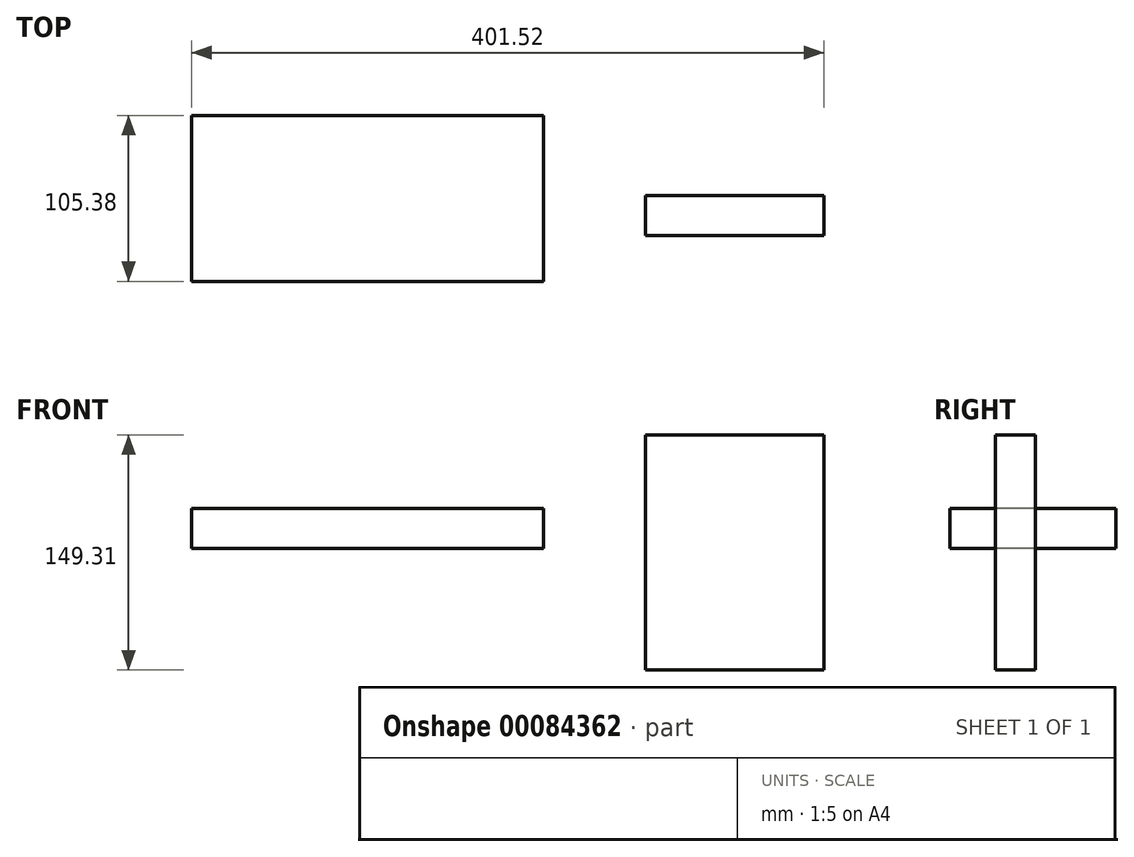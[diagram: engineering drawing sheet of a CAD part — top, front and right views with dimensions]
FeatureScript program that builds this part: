
annotation { "Feature Type Name" : "Feature", "Feature Type Description" : "" }
export const myFeature = defineFeature(function(context is Context, id is Id, definition is map)
    precondition{}
    {
        {
            var Q0;
            Q0=qCreatedBy(makeId("Top.planeOp"),FACE);
            var sketch = newSketch(context, id + "F0", { "sketchPlane" : qUnion([Q0])});
            skLineSegment(sketch, "E0.bottom", {"start": v(-112.96, 50.9) * mm, "end": v(110.6, 50.9) * mm});
            skLineSegment(sketch, "E0.top", {"start": v(-112.96, -54.48) * mm, "end": v(110.6, -54.48) * mm});
            skLineSegment(sketch, "E0.left", {"start": v(-112.96, 50.9) * mm, "end": v(-112.96, -54.48) * mm});
            skLineSegment(sketch, "E0.right", {"start": v(110.6, 50.9) * mm, "end": v(110.6, -54.48) * mm});
            skSolve(sketch);
        }
        {
            var Q0;
            Q0=makeQuery(id+"F0.imprint","IMPRINT",FACE,{"disambiguationData":[TD([[makeQuery(id+"F0.imprint","IMPRINT",EDGE,{"derivedFrom":sQuery(id+"F0.wireOp",EDGE,"E0.bottom")}),-1.0]])]});
            extrude(context, id + "F1", {"entities" : qUnion([Q0]), "depth" : 25.4 * mm});
        }
        {
            var Q0;
            Q0=qCreatedBy(makeId("Front.planeOp"),FACE);
            var sketch = newSketch(context, id + "F2", { "sketchPlane" : qUnion([Q0])});
            skLineSegment(sketch, "E1.bottom", {"start": v(175.1, 72.2) * mm, "end": v(288.56, 72.2) * mm});
            skLineSegment(sketch, "E1.top", {"start": v(175.1, -77.1) * mm, "end": v(288.56, -77.1) * mm});
            skLineSegment(sketch, "E1.left", {"start": v(175.1, 72.2) * mm, "end": v(175.1, -77.1) * mm});
            skLineSegment(sketch, "E1.right", {"start": v(288.56, 72.2) * mm, "end": v(288.56, -77.1) * mm});
            skSolve(sketch);
        }
        {
            var Q0;
            Q0=makeQuery(id+"F2.imprint","IMPRINT",FACE,{"disambiguationData":[TD([[makeQuery(id+"F2.imprint","IMPRINT",EDGE,{"derivedFrom":sQuery(id+"F2.wireOp",EDGE,"E1.bottom")}),-1.0]])]});
            extrude(context, id + "F3", {"entities" : qUnion([Q0]), "depth" : 25.4 * mm});
        }
    });
